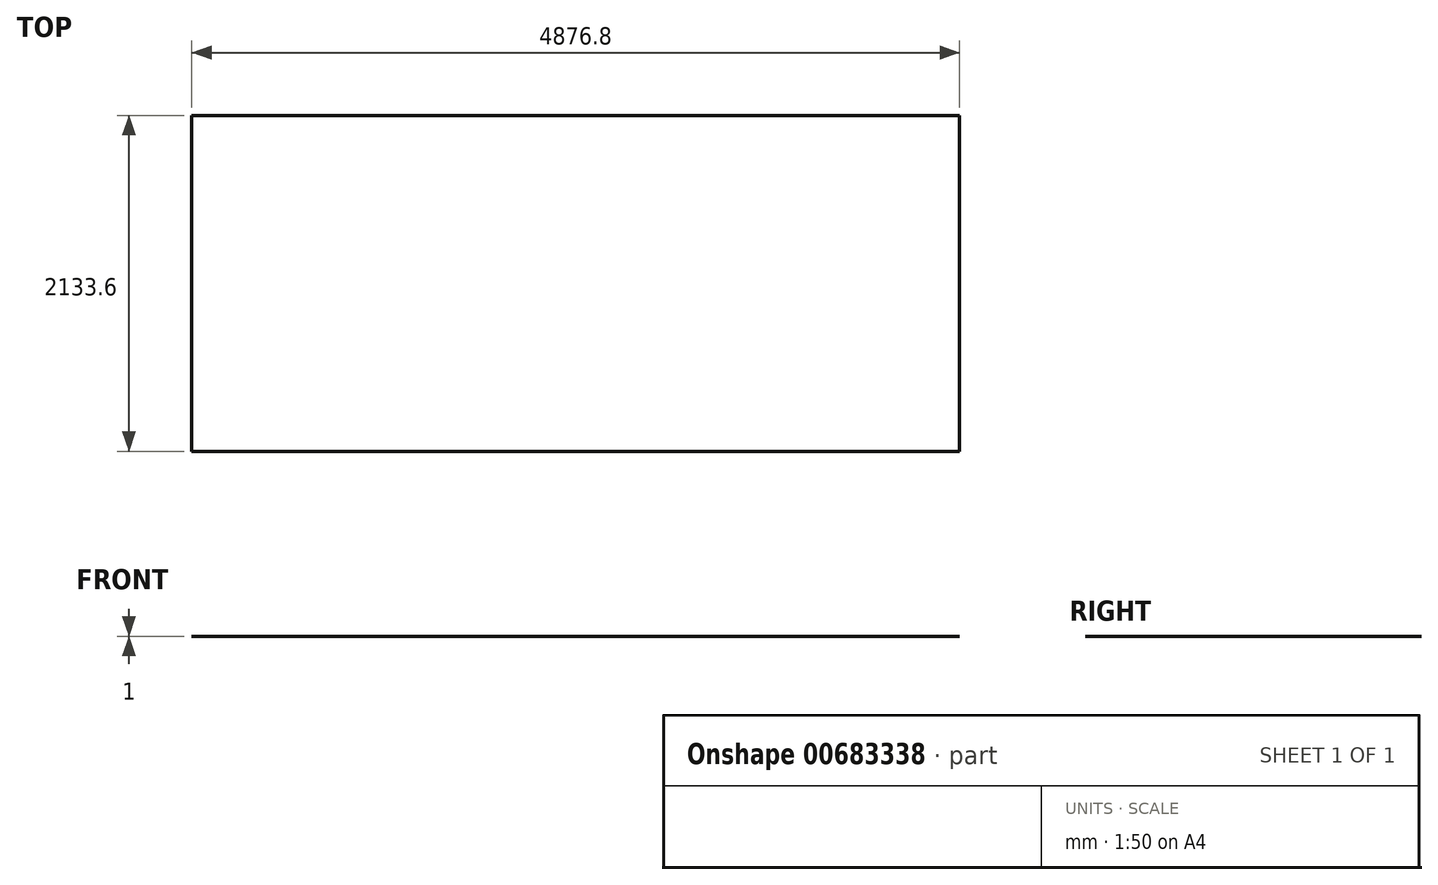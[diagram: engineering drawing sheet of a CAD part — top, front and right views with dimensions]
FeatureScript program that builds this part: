
annotation { "Feature Type Name" : "Feature", "Feature Type Description" : "" }
export const myFeature = defineFeature(function(context is Context, id is Id, definition is map)
    precondition{}
    {
        {
            var Q0;
            Q0=qCreatedBy(makeId("Top.planeOp"),FACE);
            var sketch = newSketch(context, id + "F0", { "sketchPlane" : qUnion([Q0])});
            skLineSegment(sketch, "E0.bottom", {"start": v(2438.4, 1066.8) * mm, "end": v(-2438.4, 1066.8) * mm});
            skLineSegment(sketch, "E0.top", {"start": v(2438.4, -1066.8) * mm, "end": v(-2438.4, -1066.8) * mm});
            skLineSegment(sketch, "E0.left", {"start": v(2438.4, 1066.8) * mm, "end": v(2438.4, -1066.8) * mm});
            skLineSegment(sketch, "E0.right", {"start": v(-2438.4, 1066.8) * mm, "end": v(-2438.4, -1066.8) * mm});
            skPoint(sketch, "E0.middle", {"position": v(0, 0) * mm});
            skSolve(sketch);
        }
        {
            var Q0;
            Q0=makeQuery(id+"F0.imprint","IMPRINT",FACE,{"disambiguationData":[TD([[makeQuery(id+"F0.imprint","IMPRINT",EDGE,{"derivedFrom":sQuery(id+"F0.wireOp",EDGE,"E0.bottom")}),1.0]])]});
            extrude(context, id + "F1", {"entities" : qUnion([Q0]), "oppositeDirection" : true, "depth" : 1 * mm, "offsetDistance" : 25 * mm});
        }
    });
